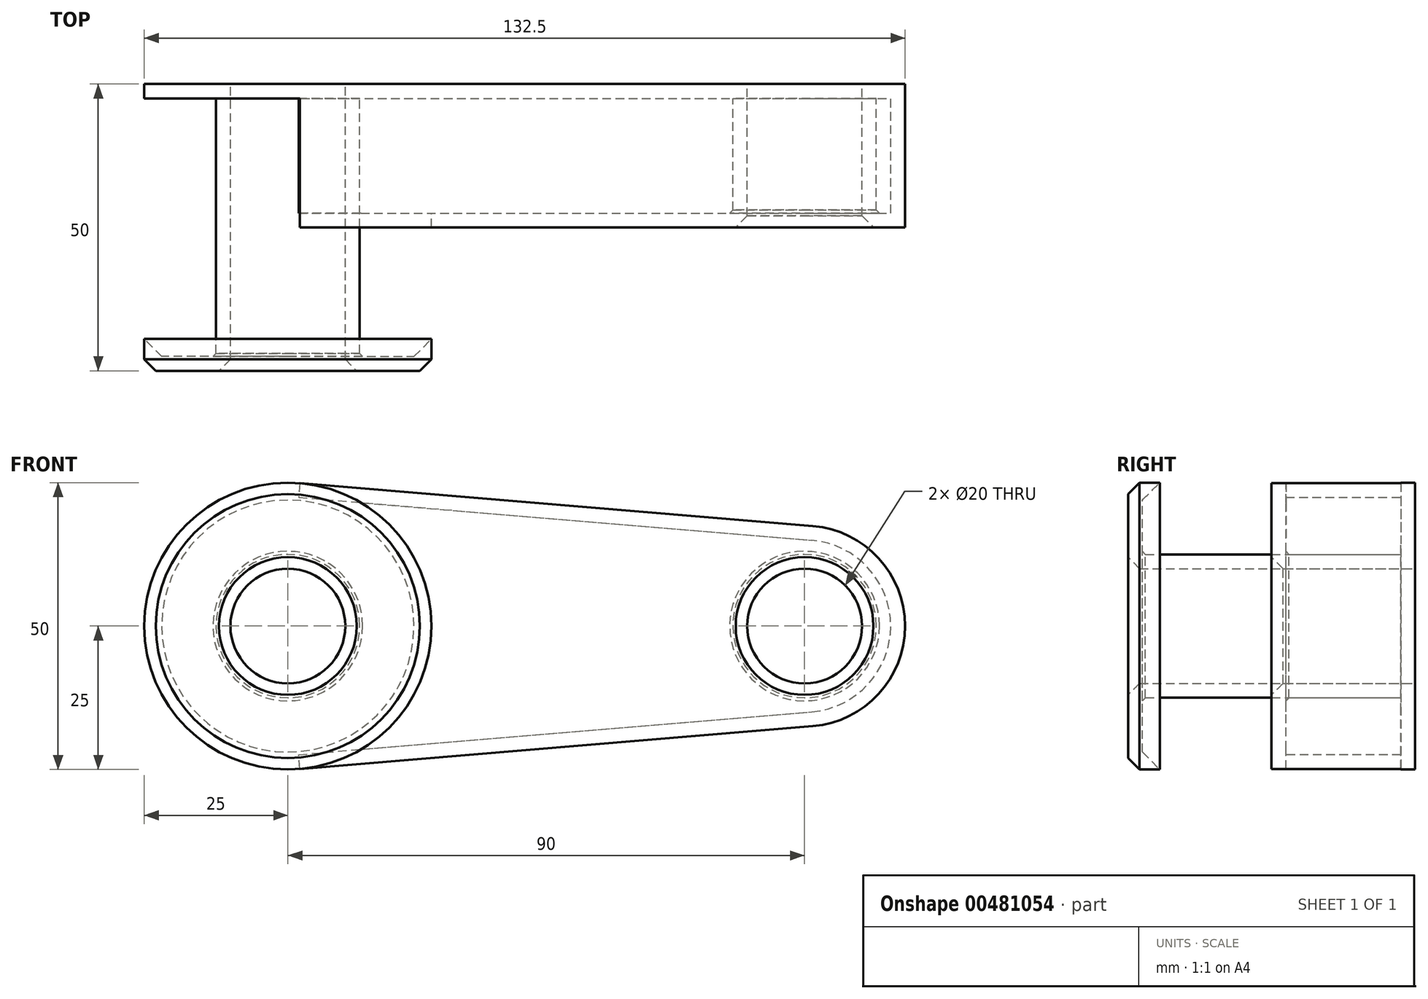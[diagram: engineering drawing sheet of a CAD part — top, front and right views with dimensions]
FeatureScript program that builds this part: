
annotation { "Feature Type Name" : "Feature", "Feature Type Description" : "" }
export const myFeature = defineFeature(function(context is Context, id is Id, definition is map)
    precondition{}
    {
        {
            var Q0;
            Q0=qCreatedBy(makeId("Front.planeOp"),FACE);
            var sketch = newSketch(context, id + "F0", { "sketchPlane" : qUnion([Q0])});
            skCircle(sketch, "E0", {"center": v(0, 0) * mm, "radius": 25 * mm});
            skCircle(sketch, "E1", {"center": v(90, 0) * mm, "radius": 17.5 * mm});
            skLineSegment(sketch, "E2", {"start": v(2.08, 24.91) * mm, "end": v(91.46, 17.44) * mm});
            skLineSegment(sketch, "E3", {"start": v(2.08, -24.91) * mm, "end": v(91.46, -17.44) * mm});
            skCircle(sketch, "E4", {"center": v(0, 0) * mm, "radius": 10 * mm});
            skCircle(sketch, "E5", {"center": v(90, 0) * mm, "radius": 10 * mm});
            skSolve(sketch);
        }
        {
            var Q0;
            Q0=qSketchRegion(id+"F0",true);
            extrude(context, id + "F1", {"entities" : qUnion([Q0]), "depth" : 25 * mm});
        }
        {
            var Q0;
            Q0=makeQuery(id+"F0.imprint","IMPRINT",FACE,{"disambiguationData":[TD([[makeQuery(id+"F0.imprint","IMPRINT",EDGE,{"derivedFrom":sQuery(id+"F0.wireOp",EDGE,"E4")}),-1.0]])]});
            extrude(context, id + "F2", {"entities" : qUnion([Q0]), "operationType" : NewBodyOperationType.ADD, "depth" : 50 * mm});
        }
        {
            var Q0;
            Q0=makeQuery(id+"F2.opExtrude","CAP_EDGE",EDGE,{"disambiguationData":[OSD([sQuery(id+"F0.wireOp",EDGE,"E0")])],"isStart":false});
            var Q1;
            Q1=makeQuery(id+"F2.opExtrude","CAP_EDGE",EDGE,{"disambiguationData":[OSD([sQuery(id+"F0.wireOp",EDGE,"E4")])],"isStart":false});
            var Q2;
            Q2=makeQuery(id+"F1.opExtrude","CAP_EDGE",EDGE,{"disambiguationData":[OSD([sQuery(id+"F0.wireOp",EDGE,"E5")])],"isStart":false});
            chamfer(context, id + "F3", {"entities" : qUnion([Q0, Q1, Q2]), "width" : 2 * mm, "tangentPropagation" : true});
        }
        {
            var Q0;
            {var subQ0=sQuery(id+"F0.wireOp",EDGE,"E0");Q0=makeQuery(id+"F2.boolean.opBoolean","MERGE",FACE,{"derivedFrom":[makeQuery(id+"F1.opExtrude","SWEPT_FACE",FACE,{"disambiguationData":[OSD([subQ0])]}),makeQuery(id+"F2.opExtrude","SWEPT_FACE",FACE,{"disambiguationData":[OSD([subQ0])]})]});}
            shell(context, id + "F4", {"entities" : qUnion([Q0]), "thickness" : 2.5 * mm});
        }
    });
